# Revit family: Скамейка стальная «Плума» Арт 12915
name_source: partatom
category: Антураж
revit_build: Autodesk Revit 2018 (Build: 20180423_1000(x64)
units: mm (PartAtom-declared; Revit-internal decimal feet)

## family parameters
Всегда вертикально = Да
Источник визуального образа = Геометрия семейства
На основе рабочей плоскости = Нет
Общий = Нет
При загрузке вырезать с полостями = Нет
Точка расчета площади = Нет

## types (3) — shared parameters
URL = https://hobbyka.ru
Артикул товара = Арт. 12915
Высота = 880 мм
Группа модели = Скамейки
Изготовитель = ООО «Хоббика»
Изображение типоразмера = Скамейка стальная «Плума» Арт 12915.jpg
Цвет лавки = Дерево
Ширина = 560 мм

## per-type parameters (varying)
| type | Версия 1,5 м | Версия 1,5 м НС | Версия 1,8 м | Длина | Материал изделия | Описание | Цвет опоры |
| Версия 1,5 м | Да | Нет | Нет | 1500 мм | Сталь, дерево | Скамейка стальная «Плума». Версия 1,5 м | Сталь |
| Версия 1,50 м. Нержавеющая сталь | Нет | Да | Нет | 1500 мм | Нержавеющая сталь, дерево | Скамейка стальная «Плума». Версия 1,5 м. Нержавеющая сталь | Нержавеющая сталь |
| Версия 1,8 м | Нет | Нет | Да | 1800 мм | Сталь, дерево | Скамейка стальная «Плума». Версия 1,8 м | Сталь |
